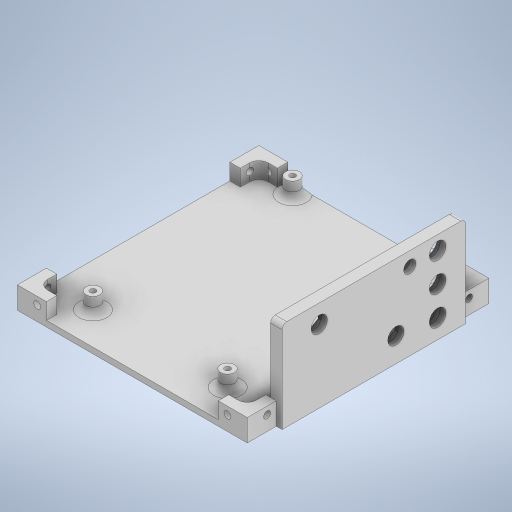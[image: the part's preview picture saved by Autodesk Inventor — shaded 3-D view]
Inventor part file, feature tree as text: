
AUTODESK INVENTOR PART (.ipt)
format: ipt  version: 2024 (Build 280153000, 153)  size: 664,064 bytes
history: native  units: in
note: dims shown in document units (in); Inventor stores cm internally (conversion verified against a paired STEP export)
features: sketch x12, extrude x11, hole x7, plane x3, fillet x2, projected_geometry x2, mirror x1
ambient origin geometry x8: Origin, YZ Plane, XZ Plane, XY Plane, X Axis, Y Axis, Z Axis, Center Point
bodies: Solid1 (feature_tree)
feature tree (38):
  sketch  "Sketch1"  dims[d0=4.0945in d1=3.8976in]
  extrude  "Extrusion1"  Depth=3.8976in
  hole  "Hole1"  [1 undecoded]
  hole  "Hole2"  [1 undecoded]
  sketch  "Sketch2"  dims[d2=0.4331in d3=1.063in]
  extrude  "Extrusion2"  Depth=0.689in
  hole  "Hole3"  [1 undecoded]
  hole  "Hole4"  [1 undecoded]
  hole  "Hole5"  [1 undecoded]
  extrude  "Extrusion3"  Depth=2.2047in
  extrude  "Extrusion4"  Depth=0.1181in
  extrude  "Extrusion5"  Depth=0.1181in
  fillet  "Fillet2"  Radius=0.1181in
  extrude  "Extrusion6"  Depth=0.1181in
  plane  "Work Plane1"
  extrude  "Extrusion7"  Depth=0.1181in
  plane  "Work Plane3"
  sketch  "Sketch8"  dims[d25=0.1378in d26=0.2362in d27=0.1575in d28=0.0787in d29=90.0deg d30=0.315in d31=0.8108in d32=0.75in]
  sketch  "Sketch9"  dims[d33=0.748in d34=2.2047in]
  plane  "Work Plane2"
  hole  "Hole6"  [1 undecoded]
  hole  "Hole7"  [1 undecoded]
  extrude  "Extrusion8"  Depth=0.0591in
  mirror  "Mirror2"
  sketch  "Sketch11"  dims[d37=0.1181in d39=1.6in d40=0.6in d42=0.1181in]
  extrude  "Extrusion9"  Depth=0.0591in
  extrude  "Extrusion10"  Depth=0.0591in
  fillet  "Fillet4"  Radius=0.0591in
  extrude  "Extrusion11"  Depth=0.0591in
  sketch  "Sketch3"  dims[d5=0.6004in d6=0.8504in]
  sketch  "Sketch4"  dims[d8=1.0591in d11=0.689in]
  sketch  "Sketch5"  dims[d12=0.1575in d13=0.1575in]
  sketch  "Sketch6"  dims[d14=0.1575in d15=0.0984in d16=0.0in]
  sketch  "Sketch7"  dims[d17=0.0984in d18=0.2362in d19=0.1575in d20=0.0787in d21=90.0deg d22=0.315in d23=0.8108in]
  sketch  "Sketch10"  dims[d35=0.1181in d36=0.4724in]
  sketch  "Sketch12"  dims[d43=0.1181in d44=0.4724in d46=0.9449in d47=0.0974in d48=0.0591in d49=0.0591in d50=0.0591in d51=0.0591in d52=0.0591in d53=0.0591in d56=0.5906in d58=1.9685in d59=0.315in d60=0.0in d61=0.0in d62=0.0591in d63=0.2362in d64=0.1575in d65=0.0787in d66=90.0deg d67=0.315in d68=0.8108in d69=0.0787in d70=0.2362in d71=0.1575in d72=0.0787in d73=90.0deg d74=0.315in d75=0.8108in d76=0.0984in d77=0.2362in d78=0.1575in d79=0.0787in d80=90.0deg d81=0.315in d82=0.8108in d83=0.1181in d84=0.0787in d86=0.0394in d87=0.0in d88=0.0in d90=0.7283in d91=3.3858in d92=2.2835in d93=0.0984in d94=0.0984in d95=0.0984in d96=0.0984in d97=0.2362in d98=0.2362in d99=0.2362in d100=0.2362in d101=0.2756in d102=0.0in d103=0.0295in d104=0.0in d108=0.0787in d109=0.0197in d110=0.0in d111=0.4921in d112=0.4921in d113=0.4921in d114=0.4921in d115=0.0197in d116=0.0in d117=0.374in d118=0.128in d119=0.1575in d120=0.128in d121=0.128in d122=0.1575in d123=0.1575in d124=0.1181in d125=0.2362in d126=0.1575in d127=0.0787in d128=90.0deg d129=0.315in d130=0.8108in d131=0.1181in d132=0.2362in d133=0.1575in d134=0.0787in d135=90.0deg d136=0.315in d137=0.8108in d138=0.315in d139=0.315in d140=0.315in d141=0.315in d142=0.1575in d143=0.3937in d144=0.0in d146=0.0787in d147=1.1469in d148=0.0394in d153=0.0787in d154=0.0984in d155=0.0in d156=0.0984in d157=0.0in d164=0.2756in d166=1.5457in d167=0.1575in d170=0.1181in d171=0.3543in d173=0.3543in d174=0.2756in d177=0.9449in d182=0.0in d184=0.0in d185=0.0in d188=0.0984in d189=1.1469in d190=0.5734in d191=0.9843in d192=0.4724in d193=0.6102in d194=0.0295in d195=0.0in d196=0.0984in d197=0.9843in d198=0.2835in d199=0.2835in d200=0.2362in d202=0.1063in d203=2.4213in d204=1.8307in d206=0.2835in d207=0.2087in d209=0.3937in d210=0.3937in d211=0.3937in d212=0.0in d214=0.315in d215=0.4724in d216=0.6299in d217=0.4724in d218=0.315in d219=0.315in d221=0.97in d222=0.97in d223=0.11in d224=0.1181in d226=0.0131in d227=0.0313in d229=0.11in d230=0.0207in d231=0.0207in]
  projected_geometry  "Projected Loop1"
  projected_geometry  "Projected Loop2"
note: 7 required parameter values undecoded (feature->parameter linkage not recoverable at this tier; creation-order binding heuristic only, values carry confidence <= 0.55)
